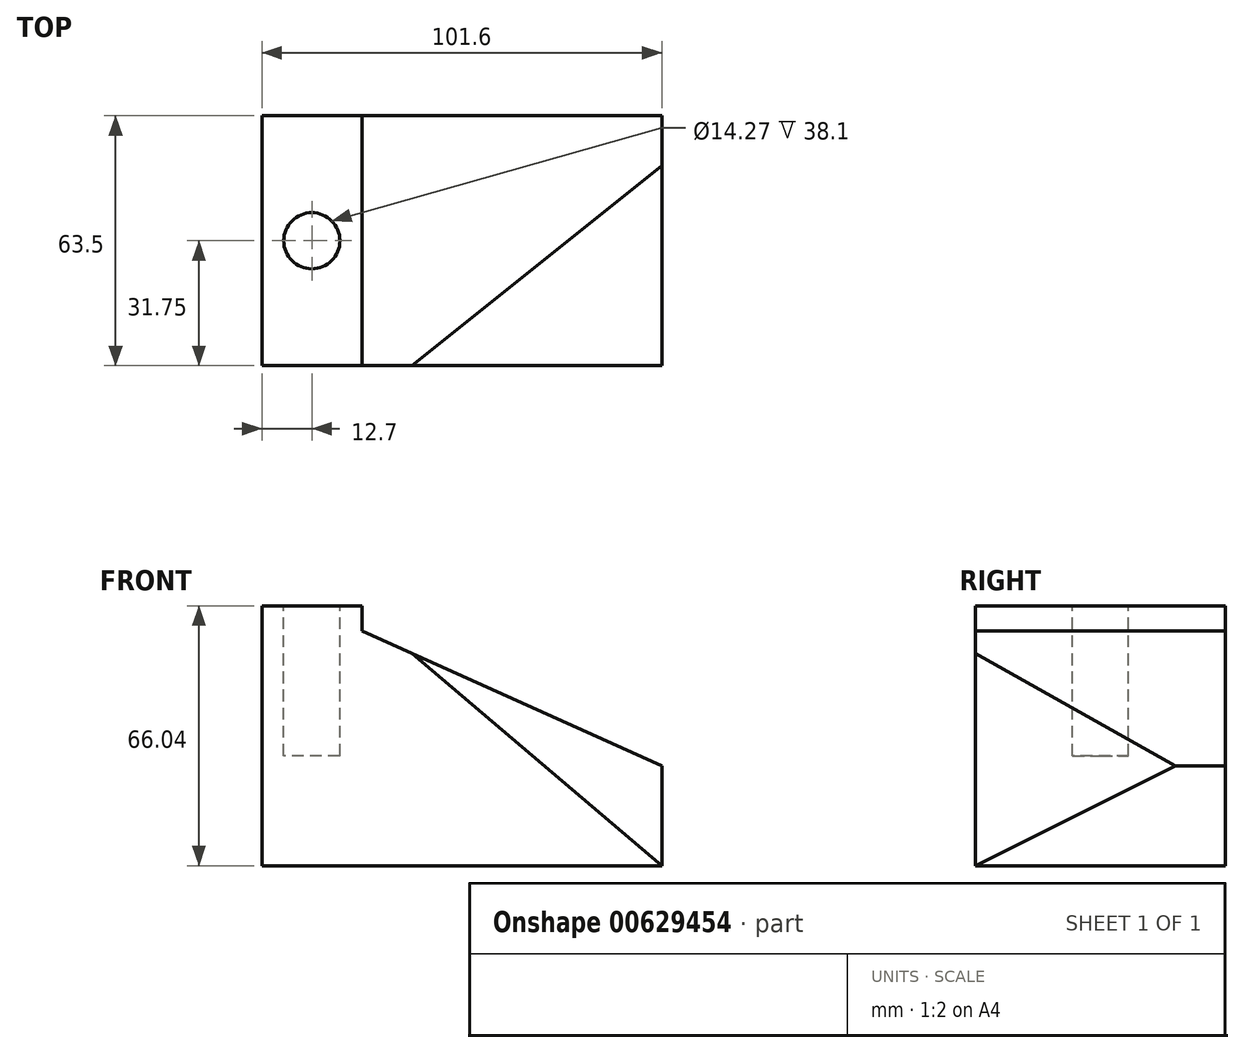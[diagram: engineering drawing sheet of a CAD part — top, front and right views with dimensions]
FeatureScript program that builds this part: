
annotation { "Feature Type Name" : "Feature", "Feature Type Description" : "" }
export const myFeature = defineFeature(function(context is Context, id is Id, definition is map)
    precondition{}
    {
        {
            var Q0;
            Q0=qCreatedBy(makeId("Front.planeOp"),FACE);
            var sketch = newSketch(context, id + "F0", { "sketchPlane" : qUnion([Q0])});
            skLineSegment(sketch, "E0", {"start": v(0, 0) * mm, "end": v(0, 66.04) * mm});
            skLineSegment(sketch, "E1", {"start": v(0, 66.04) * mm, "end": v(25.4, 66.04) * mm});
            skLineSegment(sketch, "E2", {"start": v(25.4, 66.04) * mm, "end": v(25.4, 59.7) * mm});
            skLineSegment(sketch, "E3", {"start": v(25.4, 59.7) * mm, "end": v(101.6, 25.4) * mm});
            skLineSegment(sketch, "E4", {"start": v(101.6, 25.4) * mm, "end": v(101.6, 0) * mm});
            skLineSegment(sketch, "E5", {"start": v(101.6, 0) * mm, "end": v(0, 0) * mm});
            skSolve(sketch);
        }
        {
            var Q0;
            Q0=makeQuery(id+"F0.imprint","IMPRINT",FACE,{"disambiguationData":[TD([[makeQuery(id+"F0.imprint","IMPRINT",EDGE,{"derivedFrom":sQuery(id+"F0.wireOp",EDGE,"E0")}),-1.0]])]});
            extrude(context, id + "F1", {"entities" : qUnion([Q0]), "depth" : 63.5 * mm, "offsetDistance" : 25.4 * mm, "symmetric" : true});
        }
        {
            var Q0;
            Q0=makeQuery(id+"F1.opExtrude","SWEPT_FACE",FACE,{"disambiguationData":[OSD([sQuery(id+"F0.wireOp",EDGE,"E1")])]});
            var sketch = newSketch(context, id + "F2", { "sketchPlane" : qUnion([Q0])});
            skCircle(sketch, "E6", {"center": v(12.7, 0) * mm, "radius": 7.14 * mm});
            skPoint(sketch, "E6.centerSnap0", {"position": v(0, 0) * mm});
            skSolve(sketch);
        }
        {
            var Q0;
            Q0=makeQuery(id+"F2.imprint","IMPRINT",FACE,{"disambiguationData":[TD([[makeQuery(id+"F2.imprint","IMPRINT",EDGE,{"derivedFrom":sQuery(id+"F2.wireOp",EDGE,"E6")}),1.0]])]});
            extrude(context, id + "F3", {"entities" : qUnion([Q0]), "operationType" : NewBodyOperationType.REMOVE, "oppositeDirection" : true, "depth" : 38.1 * mm, "offsetDistance" : 25.4 * mm});
        }
        {
            var Q0;
            Q0=makeQuery(id+"F1.opExtrude","SWEPT_FACE",FACE,{"disambiguationData":[OSD([sQuery(id+"F0.wireOp",EDGE,"E4")])]});
            var sketch = newSketch(context, id + "F4", { "sketchPlane" : qUnion([Q0])});
            skPoint(sketch, "E7", {"position": v(19.05, 25.4) * mm});
            skSolve(sketch);
        }
        {
            var Q0;
            Q0=makeQuery(id+"F1.opExtrude","CAP_FACE",FACE,{"disambiguationData":[OSD([sQuery(id+"F0.wireOp",EDGE,"E0"),sQuery(id+"F0.wireOp",EDGE,"E1"),sQuery(id+"F0.wireOp",EDGE,"E2"),sQuery(id+"F0.wireOp",EDGE,"E3"),sQuery(id+"F0.wireOp",EDGE,"E4"),sQuery(id+"F0.wireOp",EDGE,"E5")])],"isStart":false});
            var sketch = newSketch(context, id + "F5", { "sketchPlane" : qUnion([Q0])});
            skPoint(sketch, "E8", {"position": v(38.1, 53.98) * mm});
            skSolve(sketch);
        }
        {
            var Q0;
            Q0=sQuery(id+"F5.wireOp",VERTEX,"E8");
            var Q1;
            Q1=sQuery(id+"F4.wireOp",VERTEX,"E7");
            var Q2;
            Q2=makeQuery(id+"F1.opExtrude","CAP_VERTEX",VERTEX,{"disambiguationData":[OSD([sQuery(id+"F0.wireOp",EDGE,"E4"),sQuery(id+"F0.wireOp",EDGE,"E5")])],"isStart":false});
            cPlane(context, id + "F6", {"entities" : qUnion([Q0, Q1, Q2]), "cplaneType" : CPlaneType.THREE_POINT, "offset" : 25.4 * mm, "width" : 152.4 * mm, "height" : 152.4 * mm});
        }
        {
            var Q0;
            Q0=qCreatedBy(id+"F6.planeOp",FACE);
            var sketch = newSketch(context, id + "F7", { "sketchPlane" : qUnion([Q0])});
            skLineSegment(sketch, "E9", {"start": v(72.29, 28.4) * mm, "end": v(-7.48, -4.26) * mm});
            skLineSegment(sketch, "E10", {"start": v(-7.48, -4.26) * mm, "end": v(72.29, -28.4) * mm});
            skLineSegment(sketch, "E11", {"start": v(72.29, -28.4) * mm, "end": v(72.29, 28.4) * mm});
            skSolve(sketch);
        }
        {
            var Q0;
            Q0=makeQuery(id+"F7.imprint","IMPRINT",FACE,{"disambiguationData":[TD([[makeQuery(id+"F7.imprint","IMPRINT",EDGE,{"derivedFrom":sQuery(id+"F7.wireOp",EDGE,"E9")}),1.0]])]});
            extrude(context, id + "F8", {"entities" : qUnion([Q0]), "operationType" : NewBodyOperationType.REMOVE, "endBound" : BoundingType.THROUGH_ALL, "depth" : 25.4 * mm, "offsetDistance" : 25.4 * mm});
        }
    });
